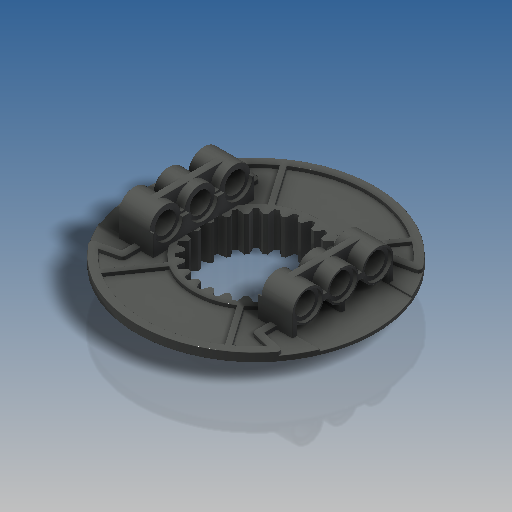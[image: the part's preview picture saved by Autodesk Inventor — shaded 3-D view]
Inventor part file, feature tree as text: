
AUTODESK INVENTOR PART (.ipt)
format: ipt  version: 2018.3 (Build 223284000, 284)  size: 1,262,592 bytes
history: native  units: in
note: dims shown in document units (in); Inventor stores cm internally (conversion verified against a paired STEP export)
features: extrude x8, sketch x6, pattern_circular x2, plane x2, revolve x1, fillet x1
ambient origin geometry x8: Origin, YZ Plane, XZ Plane, XY Plane, X Axis, Y Axis, Z Axis, Center Point
bodies: Solid1 (feature_tree)
feature tree (20):
  revolve  "Revolution1"  [1 undecoded]
  sketch  "Sketch3"  dims[d2=1.0391in d3=1.1339in]
  extrude  "Extrusion1"  Depth=1.1339in
  pattern_circular  "Circular Pattern1"  [2 undecoded]
  extrude  "Extrusion2"  Depth=0.0039in
  extrude  "Extrusion3"  Depth=0.0039in
  plane  "Work Plane1"
  sketch  "Sketch4"  dims[d4=0.0472in]
  extrude  "Extrusion4"  Depth=0.3937in TaperAngle=0.0deg
  extrude  "Extrusion6"  Depth=0.0039in TaperAngle=360.0deg
  plane  "Work Plane2"
  extrude  "Extrusion7"  Depth=0.0039in
  extrude  "Extrusion8"  Depth=0.0472in
  extrude  "Extrusion9"  Depth=0.0472in
  pattern_circular  "Circular Pattern2"  [2 undecoded]
  fillet  "Fillet1"  Radius=0.063in
  sketch  "Sketch2"  dims[d0=0.0787in d1=2.1575in]
  sketch  "Sketch5"  dims[d5=0.2362in]
  sketch  "Sketch6"  dims[d6=90.0deg]
  sketch  "Sketch7"  dims[d7=0.1018in d8=0.0299in d9=0.0632in d10=0.0515in d11=0.3937in d12=0.0in d13=9.4488in d14=360.0deg d16=2.0157in d17=0.0472in d18=0.0472in d19=0.481in d20=0.063in d21=0.063in d22=0.063in d23=0.063in d24=1.1654in d25=0.0315in d26=0.0315in d27=1.5232in d28=0.4567in d29=0.1111in d30=0.8303in d31=0.5512in d32=-0.7874in d33=0.0157in d34=0.0in d35=0.0157in d36=0.0in d37=0.2835in d38=0.189in d39=0.252in d40=0.189in d41=0.315in d42=0.0543in d43=0.2047in d44=0.2835in d45=0.0in d49=0.252in d50=0.0315in d51=0.0472in d52=0.0in d53=0.0in d54=0.0787in d55=0.063in d56=0.0315in d57=0.0in d58=0.0315in d59=0.0in d60=0.0315in d61=0.0in d62=0.7874in d63=360.0deg d65=0.5512in d66=0.0039in]
note: 5 required parameter values undecoded (feature->parameter linkage not recoverable at this tier; creation-order binding heuristic only, values carry confidence <= 0.55)